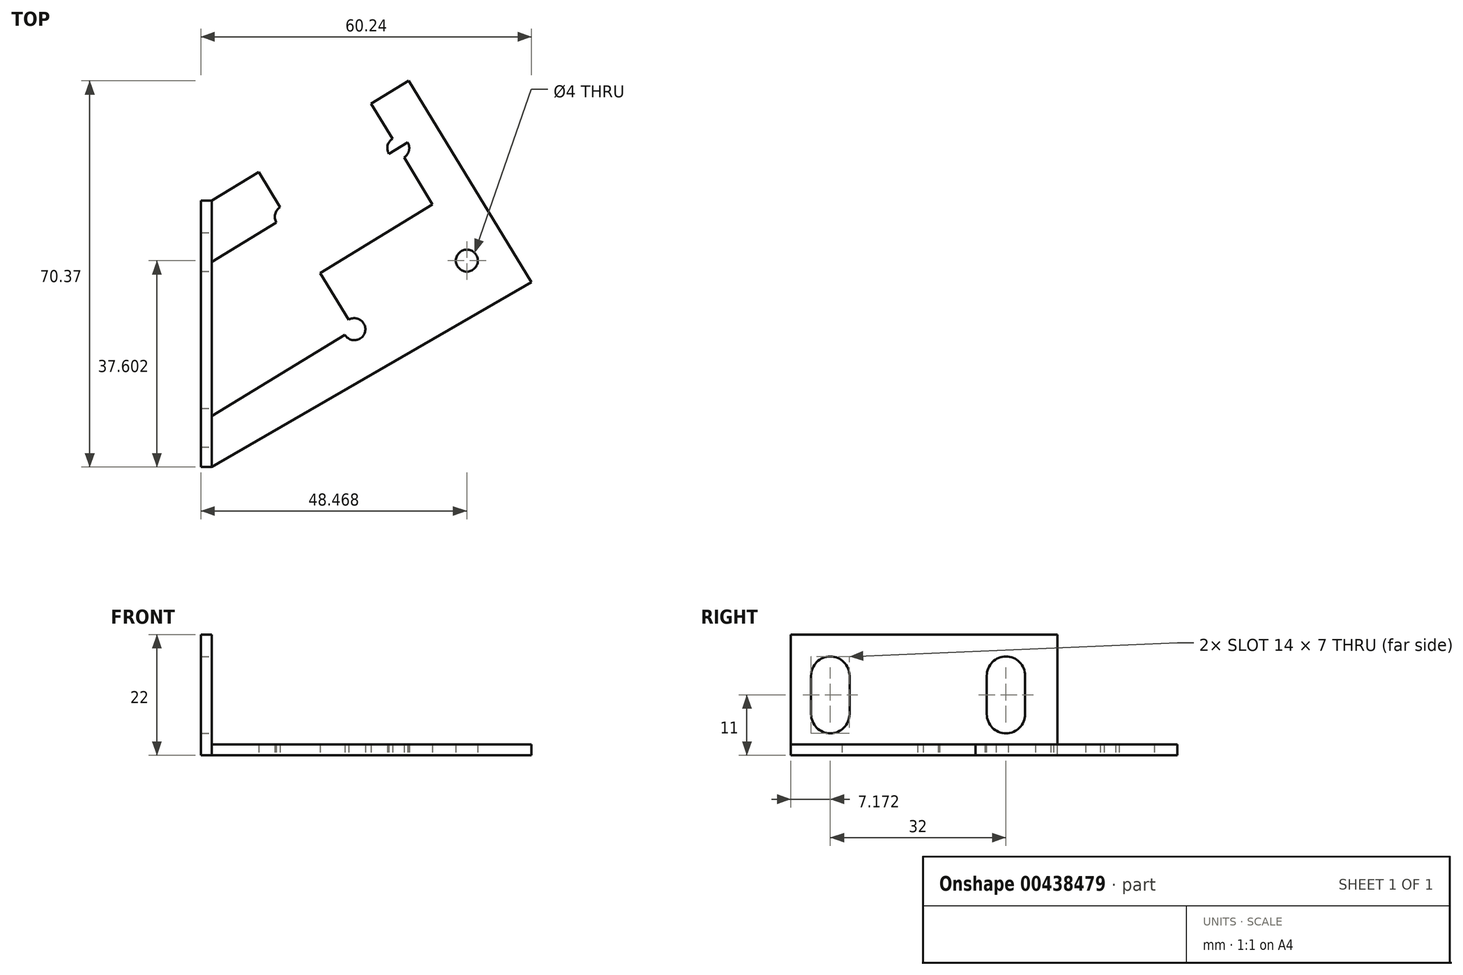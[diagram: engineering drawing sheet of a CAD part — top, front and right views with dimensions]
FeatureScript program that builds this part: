
annotation { "Feature Type Name" : "Feature", "Feature Type Description" : "" }
export const myFeature = defineFeature(function(context is Context, id is Id, definition is map)
    precondition{}
    {
        {
            var Q0;
            Q0=qCreatedBy(makeId("Top.planeOp"),FACE);
            var sketch = newSketch(context, id + "F0", { "sketchPlane" : qUnion([Q0])});
            skLineSegment(sketch, "E0", {"start": v(0, 0) * mm, "end": v(0, 48.51) * mm});
            skLineSegment(sketch, "E1", {"start": v(35.86, 70.37) * mm, "end": v(0, 48.51) * mm});
            skLineSegment(sketch, "E2.bottom", {"start": v(0, 48.51) * mm, "end": v(-2, 48.51) * mm});
            skLineSegment(sketch, "E2.top", {"start": v(0, 0) * mm, "end": v(-2, 0) * mm});
            skLineSegment(sketch, "E2.left", {"start": v(0, 48.51) * mm, "end": v(0, 0) * mm});
            skLineSegment(sketch, "E2.right", {"start": v(-2, 48.51) * mm, "end": v(-2, 0) * mm});
            skLineSegment(sketch, "E3", {"start": v(35.86, 70.37) * mm, "end": v(29.03, 66.2) * mm});
            skLineSegment(sketch, "E4", {"start": v(29.03, 66.2) * mm, "end": v(51.34, 29.61) * mm});
            skLineSegment(sketch, "E5", {"start": v(40.8, 62.26) * mm, "end": v(0, 37.39) * mm});
            skCircle(sketch, "E6", {"center": v(33.98, 58.1) * mm, "radius": 2 * mm});
            skCircle(sketch, "E7", {"center": v(46.47, 37.6) * mm, "radius": 2 * mm});
            skLineSegment(sketch, "E8", {"start": v(33.98, 58.1) * mm, "end": v(13.48, 45.6) * mm});
            skCircle(sketch, "E9", {"center": v(13.48, 45.6) * mm, "radius": 2 * mm});
            skLineSegment(sketch, "E10", {"start": v(8.54, 53.72) * mm, "end": v(30.53, 17.64) * mm});
            skLineSegment(sketch, "E11", {"start": v(35.86, 70.37) * mm, "end": v(58.24, 33.65) * mm});
            skLineSegment(sketch, "E12", {"start": v(58.24, 33.65) * mm, "end": v(0, 0) * mm});
            skLineSegment(sketch, "E13", {"start": v(53.3, 41.77) * mm, "end": v(0, 9.28) * mm});
            skLineSegment(sketch, "E14", {"start": v(53.3, 41.77) * mm, "end": v(58.24, 33.65) * mm});
            skLineSegment(sketch, "E15", {"start": v(0, 48.51) * mm, "end": v(8.54, 53.72) * mm});
            skLineSegment(sketch, "E16", {"start": v(58.24, 33.65) * mm, "end": v(58.24, 0) * mm});
            skLineSegment(sketch, "E17", {"start": v(0, 0) * mm, "end": v(58.24, 0) * mm});
            skLineSegment(sketch, "E18", {"start": v(35.86, 70.37) * mm, "end": v(47.05, 52.01) * mm});
            skLineSegment(sketch, "E19", {"start": v(35.86, 70.37) * mm, "end": v(40.8, 62.26) * mm});
            skCircle(sketch, "E20", {"center": v(25.97, 25.11) * mm, "radius": 2 * mm});
            skLineSegment(sketch, "E21", {"start": v(47.05, 52.01) * mm, "end": v(0, 23.33) * mm});
            skSolve(sketch);
        }
        {
            var Q0;
            {var subQ5=sQuery(id+"F0.wireOp",EDGE,"E3");Q0=makeQuery(id+"F0.imprint","IMPRINT",FACE,{"disambiguationData":[TD([[makeQuery(id+"F0.imprint","IMPRINT",EDGE,{"derivedFrom":subQ5}),1.0]])]});}
            var Q1;
            {var subQ1=sQuery(id+"F0.wireOp",EDGE,"E4");var subQ5=sQuery(id+"F0.wireOp",EDGE,"E6");var subQ6=makeQuery(id+"F0.imprint","INTERSECT",VERTEX,{"disambiguationData":[OD(1.0)],"derivedFrom":[subQ1,subQ5]});Q1=makeQuery(id+"F0.imprint","IMPRINT",FACE,{"disambiguationData":[TD([[makeQuery(id+"F0.imprint","IMPRINT",EDGE,{"disambiguationData":[TD([[subQ6,-1.0]])],"derivedFrom":subQ1}),1.0]])]});}
            var Q2;
            {var subQ3=sQuery(id+"F0.wireOp",EDGE,"E14");Q2=makeQuery(id+"F0.imprint","IMPRINT",FACE,{"disambiguationData":[TD([[makeQuery(id+"F0.imprint","IMPRINT",EDGE,{"derivedFrom":subQ3}),-1.0]])]});}
            var Q3;
            {var subQ0=sQuery(id+"F0.wireOp",EDGE,"E12");var subQ1=sQuery(id+"F0.wireOp",EDGE,"E4");var subQ2=makeQuery(id+"F0.imprint","INTERSECT",VERTEX,{"derivedFrom":[subQ1,subQ0]});Q3=makeQuery(id+"F0.imprint","IMPRINT",FACE,{"disambiguationData":[TD([[makeQuery(id+"F0.imprint","IMPRINT",EDGE,{"disambiguationData":[TD([[subQ2,1.0]])],"derivedFrom":subQ1}),-1.0]])]});}
            var Q4;
            {var subQ1=sQuery(id+"F0.wireOp",EDGE,"E6");var subQ6=sQuery(id+"F0.wireOp",EDGE,"E4");var subQ10=makeQuery(id+"F0.imprint","INTERSECT",VERTEX,{"disambiguationData":[OD(1.0)],"derivedFrom":[subQ6,subQ1]});Q4=makeQuery(id+"F0.imprint","IMPRINT",FACE,{"disambiguationData":[TD([[makeQuery(id+"F0.imprint","IMPRINT",EDGE,{"disambiguationData":[TD([[subQ10,-1.0]])],"derivedFrom":subQ6}),-1.0]])]});}
            var Q5;
            {var subQ1=sQuery(id+"F0.wireOp",EDGE,"E5");var subQ5=sQuery(id+"F0.wireOp",EDGE,"E2.left");var subQ6=makeQuery(id+"F0.imprint","INTERSECT",VERTEX,{"derivedFrom":[subQ5,subQ1]});Q5=makeQuery(id+"F0.imprint","IMPRINT",FACE,{"disambiguationData":[TD([[makeQuery(id+"F0.imprint","IMPRINT",EDGE,{"disambiguationData":[TD([[subQ6,-1.0]])],"derivedFrom":subQ5}),1.0]])]});}
            var Q6;
            {var subQ6=sQuery(id+"F0.wireOp",EDGE,"E1");Q6=makeQuery(id+"F0.imprint","IMPRINT",FACE,{"disambiguationData":[TD([[makeQuery(id+"F0.imprint","IMPRINT",EDGE,{"derivedFrom":subQ6}),1.0]])]});}
            var Q7;
            {var subQ0=sQuery(id+"F0.wireOp",EDGE,"E15");Q7=makeQuery(id+"F0.imprint","IMPRINT",FACE,{"disambiguationData":[TD([[makeQuery(id+"F0.imprint","IMPRINT",EDGE,{"derivedFrom":subQ0}),-1.0]])]});}
            var Q8;
            {var subQ0=sQuery(id+"F0.wireOp",EDGE,"E12");var subQ3=sQuery(id+"F0.wireOp",EDGE,"E10");var subQ4=makeQuery(id+"F0.imprint","INTERSECT",VERTEX,{"derivedFrom":[subQ3,subQ0]});Q8=makeQuery(id+"F0.imprint","IMPRINT",FACE,{"disambiguationData":[TD([[makeQuery(id+"F0.imprint","IMPRINT",EDGE,{"disambiguationData":[TD([[subQ4,1.0]])],"derivedFrom":subQ3}),-1.0]])]});}
            var Q9;
            {var subQ0=sQuery(id+"F0.wireOp",EDGE,"E11");Q9=makeQuery(id+"F0.imprint","IMPRINT",FACE,{"disambiguationData":[TD([[makeQuery(id+"F0.imprint","IMPRINT",EDGE,{"derivedFrom":subQ0}),-1.0]])]});}
            var Q10;
            {var subQ0=sQuery(id+"F0.wireOp",EDGE,"E21");var subQ9=sQuery(id+"F0.wireOp",EDGE,"E4");var subQ11=makeQuery(id+"F0.imprint","INTERSECT",VERTEX,{"derivedFrom":[subQ9,subQ0]});Q10=makeQuery(id+"F0.imprint","IMPRINT",FACE,{"disambiguationData":[TD([[makeQuery(id+"F0.imprint","IMPRINT",EDGE,{"disambiguationData":[TD([[subQ11,-1.0]])],"derivedFrom":subQ9}),-1.0]])]});}
            var Q11;
            {var subQ3=sQuery(id+"F0.wireOp",EDGE,"E13");var subQ7=sQuery(id+"F0.wireOp",EDGE,"E2.left");var subQ8=makeQuery(id+"F0.imprint","INTERSECT",VERTEX,{"derivedFrom":[subQ7,subQ3]});Q11=makeQuery(id+"F0.imprint","IMPRINT",FACE,{"disambiguationData":[TD([[makeQuery(id+"F0.imprint","IMPRINT",EDGE,{"disambiguationData":[TD([[subQ8,1.0]])],"derivedFrom":subQ7}),1.0]])]});}
            extrude(context, id + "F1", {"entities" : qUnion([Q0, Q1, Q2, Q3, Q4, Q5, Q6, Q7, Q8, Q9, Q10, Q11]), "depth" : 2 * mm});
        }
        {
            var Q0;
            Q0=qCreatedBy(makeId("Right.planeOp"),FACE);
            var sketch = newSketch(context, id + "F2", { "sketchPlane" : qUnion([Q0])});
            skLineSegment(sketch, "E22", {"start": v(23.17, 0) * mm, "end": v(23.17, 22) * mm, "construction": true});
            skLineSegment(sketch, "E23", {"start": v(23.17, 22) * mm, "end": v(39.17, 22) * mm, "construction": true});
            skLineSegment(sketch, "E24", {"start": v(23.17, 22) * mm, "end": v(7.17, 22) * mm, "construction": true});
            skLineSegment(sketch, "E25", {"start": v(7.17, 22) * mm, "end": v(7.17, 0) * mm, "construction": true});
            skLineSegment(sketch, "E26", {"start": v(39.17, 22) * mm, "end": v(39.17, 0) * mm, "construction": true});
            skLineSegment(sketch, "E27", {"start": v(48.52, 0) * mm, "end": v(48.52, 7.5) * mm, "construction": true});
            skLineSegment(sketch, "E28", {"start": v(0, 0) * mm, "end": v(0, 7.5) * mm, "construction": true});
            skLineSegment(sketch, "E29", {"start": v(48.52, 7.5) * mm, "end": v(0, 7.5) * mm, "construction": true});
            skCircle(sketch, "E30", {"center": v(39.17, 7.5) * mm, "radius": 3.5 * mm});
            skCircle(sketch, "E31", {"center": v(7.17, 7.5) * mm, "radius": 3.5 * mm});
            skLineSegment(sketch, "E32", {"start": v(31.92, 22) * mm, "end": v(31.92, 22) * mm});
            skLineSegment(sketch, "E33", {"start": v(48.52, 14.5) * mm, "end": v(0, 14.5) * mm, "construction": true});
            skCircle(sketch, "E34", {"center": v(39.17, 14.5) * mm, "radius": 3.5 * mm});
            skCircle(sketch, "E35", {"center": v(7.17, 14.5) * mm, "radius": 3.5 * mm});
            skLineSegment(sketch, "E36", {"start": v(42.67, 7.5) * mm, "end": v(42.67, 14.5) * mm});
            skLineSegment(sketch, "E37", {"start": v(35.67, 7.5) * mm, "end": v(35.67, 14.5) * mm});
            skLineSegment(sketch, "E38", {"start": v(10.67, 7.5) * mm, "end": v(10.67, 14.5) * mm});
            skLineSegment(sketch, "E39", {"start": v(3.67, 7.5) * mm, "end": v(3.67, 14.5) * mm});
            skLineSegment(sketch, "E40.bottom", {"start": v(48.52, 0) * mm, "end": v(0, 0) * mm});
            skLineSegment(sketch, "E40.top", {"start": v(48.52, 22) * mm, "end": v(0, 22) * mm});
            skLineSegment(sketch, "E40.left", {"start": v(48.52, 0) * mm, "end": v(48.52, 22) * mm});
            skLineSegment(sketch, "E40.right", {"start": v(0, 0) * mm, "end": v(0, 22) * mm});
            skLineSegment(sketch, "E41", {"start": v(7.17, 18) * mm, "end": v(0, 18) * mm, "construction": true});
            skSolve(sketch);
        }
        {
            var Q0;
            {var subQ5=sQuery(id+"F2.wireOp",EDGE,"E36");Q0=makeQuery(id+"F2.imprint","IMPRINT",FACE,{"disambiguationData":[TD([[makeQuery(id+"F2.imprint","IMPRINT",EDGE,{"derivedFrom":subQ5}),-1.0]])]});}
            extrude(context, id + "F3", {"entities" : qUnion([Q0]), "operationType" : NewBodyOperationType.ADD, "depth" : -2 * mm});
        }
    });
